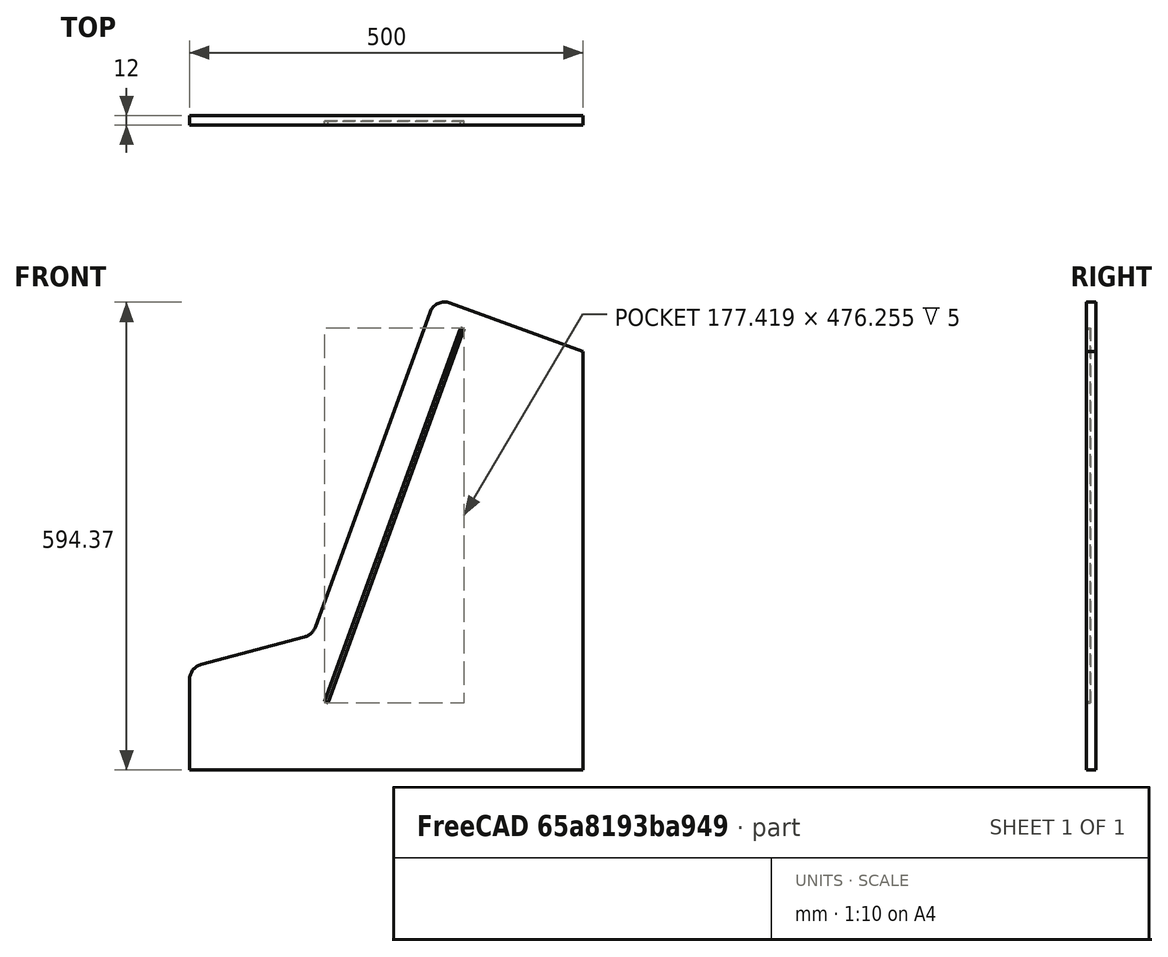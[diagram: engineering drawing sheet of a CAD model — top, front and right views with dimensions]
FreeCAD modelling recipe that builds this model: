
FCSTD DOCUMENT  (FreeCAD 0.19R24276 (Git))
Label: 9000_ASM_Profile_Sidewall
License: All rights reserved
LicenseURL: http://en.wikipedia.org/wiki/All_rights_reserved
objects: TechDraw::DrawViewDimension×11, Sketcher::SketchObject×4, PartDesign::Fillet×3, PartDesign::Pocket×2, TechDraw::DrawViewPart×2, Spreadsheet::Sheet×1, PartDesign::Pad×1, TechDraw::DrawSVGTemplate×1, TechDraw::DrawRichAnno×1, TechDraw::DrawViewAnnotation×1, TechDraw::DrawPage×1, PartDesign::Body×1
note: 17 computed .brp shape members not serialized (recipe doc carries the construction recipe); baked Part::Feature solids carry a one-line shape summary decoded from their .brp

FEATURE [Spreadsheet::Sheet] Spreadsheet  label="XLS"
  cells = B2=BODY FLOOR; E2=Ext.Ref; B3=Z=; C3(Z)=12; D3=.T; E3=Thichness; F3=16mm or 19mm for chipboard; B4=Y=; C4=500; D4=.W; E4=Width; F4=12mm for Sperholtz ; B5=X=; C5=400; D5=.D; E5=Depth; B7=Position Side Wall; D8=Left; E8=Right; B9=X0; D9(X0)==+C5; B10=Y0; C10=Y0_2; D10(Y0)==+C4; E10(Y0_2)==+D10 - D11; B11=Z0; D11(Z0)=13; B15=Position Front Wall; B16=x; C16=X0_Front; D16(X0_Front)==+H16 * abs(cos(D19)); F16=Distance on incline; G16=nS; H16(nS)=50; I16=mm; B17=y; C17=Y0_Front; D17(Y0_Front)=0; B18=z; C18=Z0_Front; D18(Z0_Front)==+H16 * abs(sin(D19)) + H18 + H20; F18=Hight of Incline; G18=nH; H18(nH)==125 + 2; I18=mm; B19=angle; C19=angley; D19(angley)=-70; F20=Thickness Material; H20=13; B22=Position Pedastil; B23=x; C23=x_pedastil; D23(x_pedastil)=0; B24=y; C24=y_pedastil; D24(y_pedastil)=0; B25=z; C25=z_pedastil; D25(z_pedastil)=-716; B27=Position Marquee; B28=x; C28==x_pedastil; B29=y; C29==y_pedastil; B30=z; C30==z_pedastil; B31=Incline
FEATURE [Sketcher::SketchObject] Sketch001
  FullyConstrained = false
  MapMode = 5
  Placement = pos=(0,0,0) rot=(1,0,0;1.5708rad)
  Support = -> [XZ_Plane]
  sketch-geometry (8):
    g0: LineSegment StartX=-20 StartY=-20 StartZ=0 EndX=-20 EndY=110 EndZ=0
    g1: LineSegment StartX=-20 StartY=110 StartZ=0 EndX=136.232 EndY=151.862 EndZ=0
    g2: LineSegment StartX=136.232 StartY=151.862 StartZ=0 EndX=292.061 EndY=580 EndZ=0
    g3: LineSegment StartX=292.061 StartY=580 StartZ=0 EndX=480 EndY=511.596 EndZ=0
    g4: LineSegment StartX=480 StartY=511.596 StartZ=0 EndX=480 EndY=-20 EndZ=0
    g5: LineSegment StartX=480 StartY=-20 StartZ=0 EndX=-20 EndY=-20 EndZ=0
    g6: GeomPoint X=91.409 Y=222.047 Z=0
    g7: GeomPoint X=-20 Y=-20 Z=0
  constraints (20):
    c: Coincident(g0,g1)
    c: Coincident(g1,g2)
    c: Coincident(g3,g4)
    c: Coincident(g4,g5)
    c: Coincident(g5,g0)
    c: Horizontal(g5)
    c: Vertical(g4)
    c: Vertical(g0)
    c: Angle(g5,g2) = 1.22173
    c: Angle(g3,g4) = 1.91986
    c: DistanceY(g4,g4) = 531.596
    c: DistanceX(g5,g5) = 500
    c: DistanceY(g0,g0) = 130
    c: Angle(g0,g1) = 1.8326
    c: Coincident(g2,g3)
    c: DistanceX(g7,g-1) = 20
    c: DistanceY(g7,g-1) = 20
    c: Coincident(g0,g7)
    c: Distance(g3) = 200
    c: DistanceY(g4,g2) = 600
FEATURE [PartDesign::Pad] Pad
  AllowMultiFace = false
  Direction = (1,1,1)
  Length = 12
  Length2 = 100
  Placement = pos=(0,0,0) rot=(1,0,0;1.5708rad)
  Profile = -> Sketch001
  Reversed = true
  Type = 0
  expr: Length = Spreadsheet.Z
FEATURE [Sketcher::SketchObject] Sketch002
  ExternalGeometry = -> [Pad]
  FullyConstrained = false
  MapMode = 5
  Placement = pos=(0,-4e-16,0) rot=(1,0,0;1.5708rad)
  Support = -> [Pad]
  sketch-geometry (12):
    g0: LineSegment StartX=465 StartY=-5 StartZ=0 EndX=465 EndY=501.093 EndZ=0
    g1: LineSegment StartX=465 StartY=501.093 StartZ=0 EndX=301.027 EndY=560.774 EndZ=0
    g2: LineSegment StartX=301.027 StartY=560.774 StartZ=0 EndX=147.657 EndY=139.394 EndZ=0
    g3: Circle CenterX=384.615 CenterY=546.313 CenterZ=0 NormalX=0 NormalY=0 NormalZ=1 AngleXU=0 Radius=15
    g4: Circle CenterX=268.58 CenterY=515.485 CenterZ=0 NormalX=0 NormalY=0 NormalZ=1 AngleXU=0 Radius=15
    g5: Circle CenterX=48.9787 CenterY=128.483 CenterZ=0 NormalX=0 NormalY=0 NormalZ=1 AngleXU=0 Radius=15
    g6: Circle CenterX=-20 CenterY=42.1215 CenterZ=0 NormalX=0 NormalY=0 NormalZ=1 AngleXU=0 Radius=15
    g7: Circle CenterX=480 CenterY=85.1486 CenterZ=0 NormalX=0 NormalY=0 NormalZ=1 AngleXU=0 Radius=15
    g8: Circle CenterX=199.413 CenterY=-20 CenterZ=0 NormalX=0 NormalY=0 NormalZ=1 AngleXU=0 Radius=15
    g9: LineSegment StartX=147.657 StartY=139.394 StartZ=0 EndX=-5 EndY=98.4901 EndZ=0
    g10: LineSegment StartX=-5 StartY=-5 StartZ=0 EndX=465 EndY=-5 EndZ=0
    g11: LineSegment StartX=-5 StartY=-5 StartZ=0 EndX=-5 EndY=98.4901 EndZ=0
  constraints (30):
    c: Vertical(g0)
    c: Coincident(g1,g0)
    c: Coincident(g2,g1)
    c: PointOnObject(g3,g-5)
    c: Radius(g3) = 15
    c: Equal(g3,g4)
    c: Tangent(g1,g3)
    c: Tangent(g2,g4)
    c: Parallel(g1,g-5)
    c: Parallel(g2,g-4)
    c: PointOnObject(g4,g-4)
    c: PointOnObject(g5,g-3)
    c: Equal(g5,g4)
    c: PointOnObject(g6,g-8)
    c: PointOnObject(g7,g-6)
    c: Equal(g5,g6)
    c: PointOnObject(g8,g-7)
    c: Equal(g6,g8)
    c: Equal(g8,g7)
    c: Tangent(g7,g0)
    c: Coincident(g9,g2)
    c: Coincident(g10,g0)
    c: Tangent(g9,g5)
    c: Tangent(g10,g8)
    c: Parallel(g-7,g10)
    c: Parallel(g9,g-3)
    c: Coincident(g11,g10)
    c: Coincident(g11,g9)
    c: Tangent(g11,g6)
    c: Vertical(g11)
FEATURE [PartDesign::Pocket] Pocket
  BaseFeature = -> Pad
  Length = 1
  Length2 = 100
  Placement = pos=(0,0,0) rot=(1,0,0;1.5708rad)
  Profile = -> Sketch002
  Reversed = true
  Type = 0
FEATURE [Sketcher::SketchObject] Sketch
  FullyConstrained = true
  MapMode = 5
  Placement = pos=(0,-4e-16,0) rot=(1,0,0;1.5708rad)
  Support = -> [Pocket]
  sketch-geometry (8):
    g0: LineSegment StartX=-20 StartY=-20 StartZ=0 EndX=480 EndY=-20 EndZ=0
    g1: LineSegment StartX=480 StartY=580 StartZ=0 EndX=-20 EndY=580 EndZ=0
    g2: LineSegment StartX=-20 StartY=580 StartZ=0 EndX=-20 EndY=-20 EndZ=0
    g3: LineSegment StartX=480 StartY=580 StartZ=0 EndX=480 EndY=-20 EndZ=0
    g4: LineSegment StartX=-30 StartY=590 StartZ=0 EndX=480 EndY=590 EndZ=0
    g5: LineSegment StartX=480 StartY=590 StartZ=0 EndX=480 EndY=-20 EndZ=0
    g6: LineSegment StartX=480 StartY=-20 StartZ=0 EndX=-30 EndY=-20 EndZ=0
    g7: LineSegment StartX=-30 StartY=-20 StartZ=0 EndX=-30 EndY=590 EndZ=0
  constraints (23):
    c: Coincident(g1,g2)
    c: Perpendicular(g1,g2)
    c: Vertical(g2)
    c: Coincident(g2,g0)
    c: Horizontal(g0)
    c: DistanceY(g2,g2) = 600
    c: DistanceX(g0,g0) = 500
    c: DistanceY(g0,g-1) = 20
    c: DistanceX(g0,g-1) = 20
    c: Coincident(g3,g1)
    c: Coincident(g3,g0)
    c: Perpendicular(g3,g1)
    c: Coincident(g4,g5)
    c: Coincident(g5,g6)
    c: Coincident(g6,g7)
    c: Coincident(g7,g4)
    c: Horizontal(g4)
    c: Horizontal(g6)
    c: Vertical(g5)
    c: Vertical(g7)
    c: Coincident(g5,g0)
    c: DistanceX(g4,g4) = 510
    c: DistanceY(g7,g7) = 610
FEATURE [PartDesign::Fillet] Fillet
  Base = -> Pocket [Edge2]
  BaseFeature = -> Pocket
  Placement = pos=(0,0,0) rot=(1,0,0;1.5708rad)
  Radius = 20
  SupportTransform = false
FEATURE [PartDesign::Fillet] Fillet001
  Base = -> Fillet [Edge25]
  BaseFeature = -> Fillet
  Placement = pos=(0,0,0) rot=(1,0,0;1.5708rad)
  Radius = 20
  SupportTransform = false
FEATURE [PartDesign::Fillet] Fillet002
  Base = -> Fillet001 [Edge22]
  BaseFeature = -> Fillet001
  Placement = pos=(0,0,0) rot=(1,0,0;1.5708rad)
  Radius = 20
  SupportTransform = false
FEATURE [TechDraw::DrawSVGTemplate] Template
  EditableTexts = Designed_by_Name=RIP; Drawing_number=9000 series; FC-Date=20210423; FC-SC=0,2; FC-SH=1/1; FC-Title=Cabinet Sidewall Profiled; Subtitle=600 x 500; Weight=Weight
  Height = 210
  Orientation = 1
  Width = 297
FEATURE [TechDraw::DrawRichAnno] RichTextAnnotation
  AnnoText = <!DOCTYPE HTML PUBLIC "-//W3C//DTD HTML 4.0//EN" "http://www.w3.org/TR/REC-html40/strict.dtd">\n<html><head><meta name="qrichtext" content="1" /><style type="text/css">\np, li { white-space: pre-wrap; }\n</style></head><body style=" font-family:'MS Shell Dlg 2'; font-size:8.25pt; font-weight:400; font-style:normal;">\n<p style="-qt-paragraph-type:empty; margin-top:0px; margin-bottom:0px; margin-left:0px; margin-right:0px; -qt-block-indent:0; text-indent:0px;"><br /></p></body></html>
  LockPosition = false
  MaxWidth = -1
  Rotation = 0
  ScaleType = 0
  ShowFrame = false
  X = 148.5
  Y = 105
FEATURE [TechDraw::DrawViewAnnotation] Annotation  label="12"
  Font = DejaVu Sans
  LineSpace = 80
  LockPosition = false
  MaxWidth = -1
  Rotation = 0
  ScaleType = 0
  Text = Thickness |  t =
  TextSize = 4
  TextStyle = 0
  X = 47.5603
  Y = 174.773
  expr: Label = <<XLS>>.Z
FEATURE [TechDraw::DrawViewPart] View
  CoarseView = false
  Direction = (0,-2,0)
  Focus = 100
  HardHidden = false
  IsoCount = 0
  IsoHidden = false
  IsoVisible = false
  LockPosition = false
  Perspective = false
  Rotation = 0
  Scale = 0.2
  ScaleType = 0
  SeamHidden = false
  SeamVisible = true
  SmoothHidden = false
  SmoothVisible = true
  Source = -> [Pocket]
  X = 84.4442
  XDirection = (1,0,0)
  Y = 124.709
FEATURE [TechDraw::DrawViewPart] View001
  CoarseView = false
  Direction = (0,-1,0)
  Focus = 100
  HardHidden = false
  IsoCount = 0
  IsoHidden = false
  IsoVisible = false
  LockPosition = false
  Perspective = false
  Rotation = 0
  Scale = 0.2
  ScaleType = 0
  SeamHidden = false
  SeamVisible = true
  SmoothHidden = false
  SmoothVisible = true
  Source = -> [Fillet002]
  X = 230.477
  XDirection = (0.263711,0.964602,0)
  Y = 124.82
FEATURE [TechDraw::DrawViewDimension] Dimension
  Arbitrary = false
  ArbitraryTolerances = false
  EqualTolerance = true
  FormatSpec = %.2f
  FormatSpecOverTolerance = %+.2f
  FormatSpecUnderTolerance = %+.2f
  Inverted = false
  LockPosition = false
  MeasureType = 1
  OverTolerance = 0
  References2D = -> [View]
  Rotation = 0
  ScaleType = 0
  TheoreticalExact = false
  Type = 2
  UnderTolerance = 0
  X = -42.5446
  Y = -13.0866
FEATURE [TechDraw::DrawViewDimension] Dimension001
  Arbitrary = false
  ArbitraryTolerances = false
  EqualTolerance = true
  FormatSpec = %.2f
  FormatSpecOverTolerance = %+.2f
  FormatSpecUnderTolerance = %+.2f
  Inverted = false
  LockPosition = false
  MeasureType = 1
  OverTolerance = 0
  References2D = -> [View]
  Rotation = 0
  ScaleType = 0
  TheoreticalExact = false
  Type = 2
  UnderTolerance = 0
  X = -68.7129
  Y = -47.5941
FEATURE [TechDraw::DrawViewDimension] Dimension002
  Arbitrary = false
  ArbitraryTolerances = false
  EqualTolerance = true
  FormatSpec = %.2f
  FormatSpecOverTolerance = %+.2f
  FormatSpecUnderTolerance = %+.2f
  Inverted = false
  LockPosition = false
  MeasureType = 1
  OverTolerance = 0
  References2D = -> [View]
  Rotation = 0
  ScaleType = 0
  TheoreticalExact = false
  Type = 1
  UnderTolerance = 0
  X = -2.37624
  Y = -88.8119
FEATURE [TechDraw::DrawViewDimension] Dimension003
  Arbitrary = false
  ArbitraryTolerances = false
  EqualTolerance = true
  FormatSpec = %.2f
  FormatSpecOverTolerance = %+.2f
  FormatSpecUnderTolerance = %+.2f
  Inverted = false
  LockPosition = false
  MeasureType = 1
  OverTolerance = 0
  References2D = -> [View]
  Rotation = 0
  ScaleType = 0
  TheoreticalExact = false
  Type = 1
  UnderTolerance = 0
  X = 2.9703
  Y = -45.4158
FEATURE [TechDraw::DrawViewDimension] Dimension004
  Arbitrary = false
  ArbitraryTolerances = false
  EqualTolerance = true
  FormatSpec = %.2f
  FormatSpecOverTolerance = %+.2f
  FormatSpecUnderTolerance = %+.2f
  Inverted = false
  LockPosition = false
  MeasureType = 1
  OverTolerance = 0
  References2D = -> [View]
  Rotation = 0
  ScaleType = 0
  TheoreticalExact = false
  Type = 2
  UnderTolerance = 0
  X = 59.4752
  Y = -6.74715
FEATURE [TechDraw::DrawViewDimension] Dimension005
  Arbitrary = false
  ArbitraryTolerances = false
  EqualTolerance = true
  FormatSpec = %.2f
  FormatSpecOverTolerance = %+.2f
  FormatSpecUnderTolerance = %+.2f
  Inverted = false
  LockPosition = false
  MeasureType = 1
  OverTolerance = 0
  References2D = -> [View]
  Rotation = 0
  ScaleType = 0
  TheoreticalExact = false
  Type = 2
  UnderTolerance = 0
  X = 81.1071
  Y = -1.78218
FEATURE [TechDraw::DrawViewDimension] Dimension006
  Arbitrary = false
  ArbitraryTolerances = false
  EqualTolerance = true
  FormatSpec = %.2f
  FormatSpecOverTolerance = %+.2f
  FormatSpecUnderTolerance = %+.2f
  Inverted = false
  LockPosition = false
  MeasureType = 1
  OverTolerance = 0
  References2D = -> [View]
  Rotation = 0
  ScaleType = 0
  TheoreticalExact = false
  Type = 0
  UnderTolerance = 0
  X = 37.2033
  Y = 68.5448
FEATURE [TechDraw::DrawViewDimension] Dimension007
  Arbitrary = false
  ArbitraryTolerances = false
  EqualTolerance = true
  FormatSpec = R%.2f
  FormatSpecOverTolerance = %+.2f
  FormatSpecUnderTolerance = %+.2f
  Inverted = false
  LockPosition = false
  MeasureType = 1
  OverTolerance = 0
  References2D = -> [View001]
  Rotation = 0
  ScaleType = 0
  TheoreticalExact = false
  Type = 4
  UnderTolerance = 0
  X = 26.6811
  Y = 32.8634
FEATURE [TechDraw::DrawViewDimension] Dimension008
  Arbitrary = false
  ArbitraryTolerances = false
  EqualTolerance = true
  FormatSpec = R%.2f
  FormatSpecOverTolerance = %+.2f
  FormatSpecUnderTolerance = %+.2f
  Inverted = false
  LockPosition = false
  MeasureType = 1
  OverTolerance = 0
  References2D = -> [View001]
  Rotation = 0
  ScaleType = 0
  TheoreticalExact = false
  Type = 4
  UnderTolerance = 0
  X = -34.8156
  Y = -2.92842
FEATURE [TechDraw::DrawViewDimension] Dimension009
  Arbitrary = false
  ArbitraryTolerances = false
  EqualTolerance = true
  FormatSpec = R%.2f
  FormatSpecOverTolerance = %+.2f
  FormatSpecUnderTolerance = %+.2f
  Inverted = false
  LockPosition = false
  MeasureType = 1
  OverTolerance = 0
  References2D = -> [View001]
  Rotation = 0
  ScaleType = 0
  TheoreticalExact = false
  Type = 4
  UnderTolerance = 0
  X = -31.5618
  Y = -40.6725
FEATURE [TechDraw::DrawViewDimension] Dimension010
  Arbitrary = false
  ArbitraryTolerances = false
  EqualTolerance = true
  FormatSpec = %.2f
  FormatSpecOverTolerance = %+.2f
  FormatSpecUnderTolerance = %+.2f
  Inverted = false
  LockPosition = false
  MeasureType = 1
  OverTolerance = 0
  References2D = -> [View]
  Rotation = 0
  ScaleType = 0
  TheoreticalExact = false
  Type = 2
  UnderTolerance = 0
  X = 30.2787
  Y = -34.7473
FEATURE [TechDraw::DrawPage] Page
  KeepUpdated = true
  NextBalloonIndex = 1
  ProjectionType = 0
  Template = -> Template
  Views = -> [RichTextAnnotation,Annotation,View,View001,Dimension,Dimension001,Dimension002,Dimension003,Dimension004,Dimension005,Dimension006,Dimension007,Dimension008,Dimension009,Dimension010]
FEATURE [Sketcher::SketchObject] Sketch003
  ExternalGeometry = -> [Pocket]
  FullyConstrained = true
  MapMode = 5
  Placement = pos=(0,-4e-16,0) rot=(1,0,0;1.5708rad)
  Support = -> [Pocket]
  sketch-geometry (8):
    g0: LineSegment StartX=480 StartY=511.596 StartZ=0 EndX=337.379 EndY=563.506 EndZ=0
    g1: LineSegment StartX=480 StartY=-20 StartZ=0 EndX=125 EndY=-20 EndZ=0
    g2: LineSegment StartX=337.379 StartY=563.506 StartZ=0 EndX=328.828 EndY=540.014 EndZ=0
    g3: LineSegment StartX=328.828 StartY=540.014 StartZ=0 EndX=156.108 EndY=65.4688 EndZ=0
    g4: LineSegment StartX=156.108 StartY=65.4688 StartZ=0 EndX=125 EndY=-20 EndZ=0
    g5: LineSegment StartX=156.108 StartY=65.4688 StartZ=0 EndX=151.41 EndY=67.1789 EndZ=0
    g6: LineSegment StartX=151.41 StartY=67.1789 StartZ=0 EndX=324.13 EndY=541.724 EndZ=0
    g7: LineSegment StartX=324.13 StartY=541.724 StartZ=0 EndX=328.828 EndY=540.014 EndZ=0
  constraints (22):
    c: Coincident(g0,g-5)
    c: PointOnObject(g0,g-5)
    c: Coincident(g1,g-3)
    c: Horizontal(g1)
    c: DistanceX(g1,g1) = 355
    c: Coincident(g2,g0)
    c: Coincident(g3,g2)
    c: Coincident(g4,g3)
    c: Coincident(g4,g1)
    c: Parallel(g4,g3)
    c: Parallel(g3,g2)
    c: Distance(g3) = 505
    c: Distance(g2) = 25
    c: Coincident(g5,g3)
    c: Coincident(g6,g5)
    c: Coincident(g7,g6)
    c: Coincident(g7,g3)
    c: Equal(g7,g5)
    c: Perpendicular(g3,g7)
    c: Equal(g6,g3)
    c: Distance(g5) = 5
    c: Angle(g1,g4) = 1.22173
FEATURE [PartDesign::Pocket] Pocket001
  BaseFeature = -> Fillet002
  Length = 5
  Length2 = 100
  Placement = pos=(0,0,0) rot=(1,0,0;1.5708rad)
  Profile = -> Sketch003
  Type = 0
FEATURE [PartDesign::Body] Body
  Group = -> [Sketch001,Pad,Sketch002,Pocket,Fillet,Fillet001,Fillet002,Sketch003,Pocket001]
  Origin = -> Origin
  Tip = -> Pocket001
